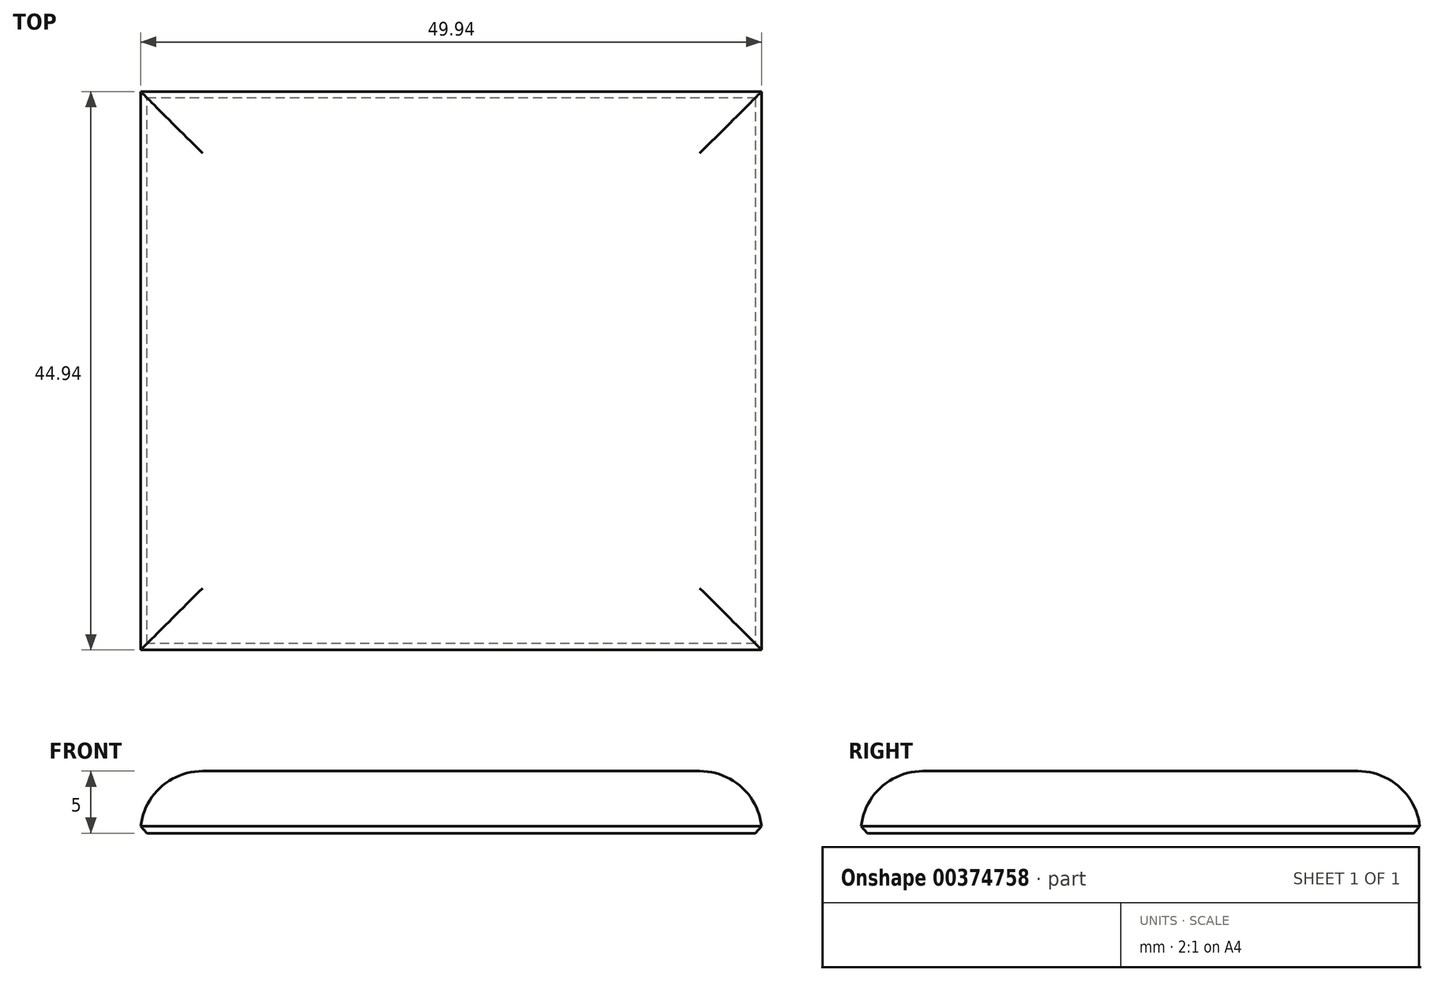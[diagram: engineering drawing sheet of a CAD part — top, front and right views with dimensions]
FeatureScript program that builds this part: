
annotation { "Feature Type Name" : "Feature", "Feature Type Description" : "" }
export const myFeature = defineFeature(function(context is Context, id is Id, definition is map)
    precondition{}
    {
        {
            var Q0;
            Q0=qCreatedBy(makeId("Top.planeOp"),FACE);
            var sketch = newSketch(context, id + "F0", { "sketchPlane" : qUnion([Q0])});
            skLineSegment(sketch, "E0.bottom", {"start": v(0, 0) * mm, "end": v(50, 0) * mm});
            skLineSegment(sketch, "E0.top", {"start": v(0, 45) * mm, "end": v(50, 45) * mm});
            skLineSegment(sketch, "E0.left", {"start": v(0, 0) * mm, "end": v(0, 45) * mm});
            skLineSegment(sketch, "E0.right", {"start": v(50, 0) * mm, "end": v(50, 45) * mm});
            skSolve(sketch);
        }
        {
            var Q0;
            Q0 = qSketchRegion(id + "F0", true);
            extrude(context, id + "F1", {"entities" : qUnion([Q0]), "depth" : 5 * mm});
        }
        {
            var Q0;
            Q0=makeQuery(id+"F1.opExtrude","CAP_EDGE",EDGE,{"disambiguationData":[OSD([sQuery(id+"F0.wireOp",EDGE,"E0.left")])],"isStart":false});
            var Q1;
            Q1=makeQuery(id+"F1.opExtrude","CAP_EDGE",EDGE,{"disambiguationData":[OSD([sQuery(id+"F0.wireOp",EDGE,"E0.right")])],"isStart":false});
            var Q2;
            Q2=makeQuery(id+"F1.opExtrude","CAP_EDGE",EDGE,{"disambiguationData":[OSD([sQuery(id+"F0.wireOp",EDGE,"E0.top")])],"isStart":false});
            var Q3;
            Q3=makeQuery(id+"F1.opExtrude","CAP_EDGE",EDGE,{"disambiguationData":[OSD([sQuery(id+"F0.wireOp",EDGE,"E0.bottom")])],"isStart":false});
            fillet(context, id + "F2", {"entities" : qUnion([Q0, Q1, Q2, Q3]), "radius" : 5 * mm, "tangentPropagation" : true, "allowEdgeOverflow" : false});
        }
        {
            var Q0;
            Q0=makeQuery(id+"F1.opExtrude","CAP_FACE",FACE,{"disambiguationData":[OSD([sQuery(id+"F0.wireOp",EDGE,"E0.bottom"),sQuery(id+"F0.wireOp",EDGE,"E0.top"),sQuery(id+"F0.wireOp",EDGE,"E0.left"),sQuery(id+"F0.wireOp",EDGE,"E0.right")])],"isStart":true});
            chamfer(context, id + "F3", {"entities" : qUnion([Q0]), "width" : .5 * mm, "tangentPropagation" : true});
        }
    });
